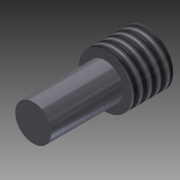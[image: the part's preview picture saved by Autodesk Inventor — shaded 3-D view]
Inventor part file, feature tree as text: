
AUTODESK INVENTOR PART (.ipt)
format: ipt  version: 2012 (Build 160160000, 160)  size: 86,528 bytes
history: native  units: in
note: dims shown in document units (in); Inventor stores cm internally (conversion verified against a paired STEP export)
features: extrude x2, sketch x1, thread x1
ambient origin geometry x8: Origin, YZ Plane, XZ Plane, XY Plane, X Axis, Y Axis, Z Axis, Center Point
bodies: Solid1 (feature_tree)
feature tree (4):
  sketch  "Sketch1"  dims[d0=0.366in d1=0.25in d2=0.288in d3=0.0in d4=0.5in d5=0.0in d6=1.0in d7=0.0in]
  extrude  "Extrusion1"  Depth=0.25in
  extrude  "Extrusion2"  Depth=0.288in TaperAngle=0.0deg
  thread  "Thread1"  [1 undecoded]
note: 1 required parameter value undecoded (feature->parameter linkage not recoverable at this tier; creation-order binding heuristic only, values carry confidence <= 0.55)
